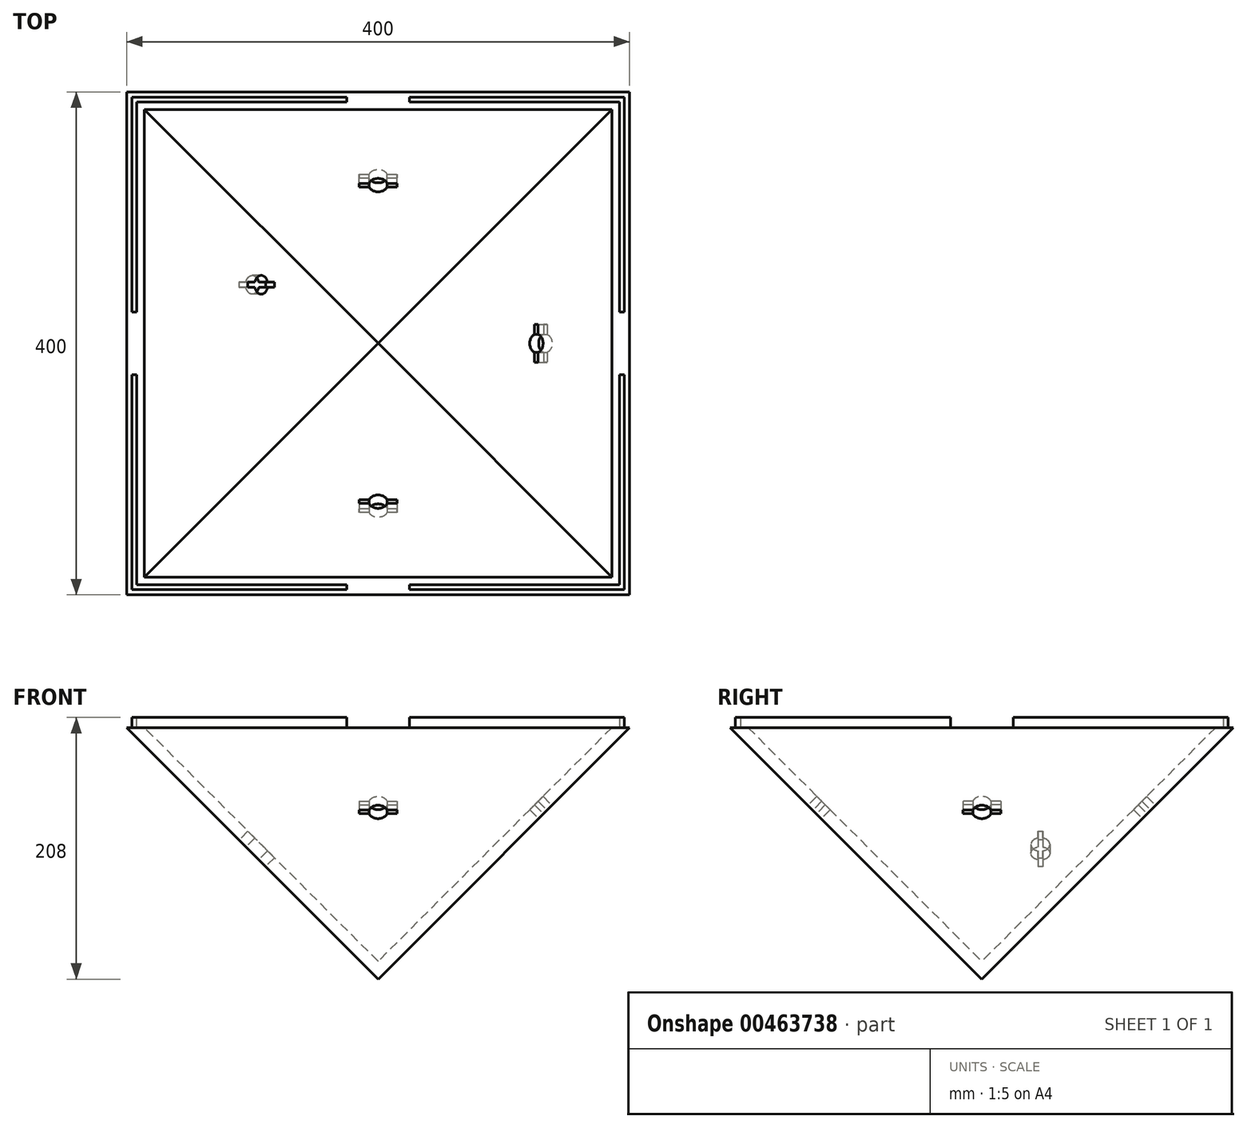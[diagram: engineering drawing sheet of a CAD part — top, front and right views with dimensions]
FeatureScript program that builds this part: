
annotation { "Feature Type Name" : "Feature", "Feature Type Description" : "" }
export const myFeature = defineFeature(function(context is Context, id is Id, definition is map)
    precondition{}
    {
        {
            var Q0;
            Q0=qCreatedBy(makeId("Top.planeOp"),FACE);
            var sketch = newSketch(context, id + "F0", { "sketchPlane" : qUnion([Q0])});
            skLineSegment(sketch, "E0.bottom", {"start": v(-200, 200) * mm, "end": v(200, 200) * mm});
            skLineSegment(sketch, "E0.top", {"start": v(-200, -200) * mm, "end": v(200, -200) * mm});
            skLineSegment(sketch, "E0.left", {"start": v(-200, 200) * mm, "end": v(-200, -200) * mm});
            skLineSegment(sketch, "E0.right", {"start": v(200, 200) * mm, "end": v(200, -200) * mm});
            skPoint(sketch, "E0.middle", {"position": v(0, 0) * mm});
            skSolve(sketch);
        }
        {
            var Q0;
            Q0=qCreatedBy(makeId("Front.planeOp"),FACE);
            var sketch = newSketch(context, id + "F1", { "sketchPlane" : qUnion([Q0])});
            skLineSegment(sketch, "E1", {"start": v(0, 0) * mm, "end": v(-200, 0) * mm});
            skLineSegment(sketch, "E2", {"start": v(0, 0) * mm, "end": v(0, -200) * mm});
            skLineSegment(sketch, "E3", {"start": v(0, -200) * mm, "end": v(-200, 0) * mm});
            skSolve(sketch);
        }
        {
            var Q0;
            Q0=makeQuery(id+"F0.imprint","IMPRINT",FACE,{"disambiguationData":[TD([[makeQuery(id+"F0.imprint","IMPRINT",EDGE,{"derivedFrom":sQuery(id+"F0.wireOp",EDGE,"E0.bottom")}),-1.0]])]});
            var Q1;
            Q1=sQuery(id+"F1.wireOp",VERTEX,"E3.start");
            loft(context, id + "F2", {"sheetProfilesArray" : [{ "sheetProfileEntities" : qUnion([Q0]) }, { "sheetProfileEntities" : qUnion([Q1]) }]});
        }
        {
            var Q0;
            Q0=makeQuery(id+"F2.opLoft","CAP_FACE",FACE,{"disambiguationData":[OSD([makeQuery(id+"F0.imprint","IMPRINT",FACE,{"disambiguationData":[TD([[makeQuery(id+"F0.imprint","IMPRINT",EDGE,{"derivedFrom":sQuery(id+"F0.wireOp",EDGE,"E0.bottom")}),-1.0]])]})])],"isStart":true});
            shell(context, id + "F3", {"entities" : qUnion([Q0]), "thickness" : 10 * mm});
        }
        {
            var Q0;
            Q0=makeQuery(id+"F0.imprint","IMPRINT",FACE,{"disambiguationData":[TD([[makeQuery(id+"F0.imprint","IMPRINT",EDGE,{"derivedFrom":sQuery(id+"F0.wireOp",EDGE,"E0.bottom")}),-1.0]])]});
            var sketch = newSketch(context, id + "F4", { "sketchPlane" : qUnion([Q0])});
            skLineSegment(sketch, "E4.0", {"start": v(-191.86, 191.86) * mm, "end": v(191.86, 191.86) * mm});
            skLineSegment(sketch, "E4.1", {"start": v(-191.86, -191.86) * mm, "end": v(-191.86, 191.86) * mm});
            skLineSegment(sketch, "E4.2", {"start": v(191.86, -191.86) * mm, "end": v(-191.86, -191.86) * mm});
            skLineSegment(sketch, "E4.3", {"start": v(191.86, 191.86) * mm, "end": v(191.86, -191.86) * mm});
            skLineSegment(sketch, "E5.0", {"start": v(-195.86, 195.86) * mm, "end": v(195.86, 195.86) * mm});
            skLineSegment(sketch, "E5.1", {"start": v(-195.86, -195.86) * mm, "end": v(-195.86, 195.86) * mm});
            skLineSegment(sketch, "E5.2", {"start": v(195.86, -195.86) * mm, "end": v(-195.86, -195.86) * mm});
            skLineSegment(sketch, "E5.3", {"start": v(195.86, 195.86) * mm, "end": v(195.86, -195.86) * mm});
            skSolve(sketch);
        }
        {
            var Q0;
            Q0=makeQuery(id+"F4.imprint","IMPRINT",FACE,{"disambiguationData":[TD([[makeQuery(id+"F4.imprint","IMPRINT",EDGE,{"derivedFrom":sQuery(id+"F4.wireOp",EDGE,"E4.0")}),1.0]])]});
            extrude(context, id + "F5", {"entities" : qUnion([Q0]), "operationType" : NewBodyOperationType.ADD, "depth" : 8 * mm});
        }
        {
            var Q0;
            Q0=makeQuery(id+"F2.opLoft","SWEPT_FACE",FACE,{"disambiguationData":[OSD([sQuery(id+"F0.wireOp",EDGE,"E0.top"),sQuery(id+"F0.wireOp",EDGE,"E0.left"),sQuery(id+"F0.wireOp",EDGE,"E0.right")])]});
            var sketch = newSketch(context, id + "F6", { "sketchPlane" : qUnion([Q0])});
            skLineSegment(sketch, "E6", {"start": v(0, -141.42) * mm, "end": v(0, 46.58) * mm});
            skLineSegment(sketch, "E7", {"start": v(0, 46.58) * mm, "end": v(7.5, 46.58) * mm});
            skCircle(sketch, "E8", {"center": v(0, 46.58) * mm, "radius": 7.5 * mm});
            skLineSegment(sketch, "E9.bottom", {"start": v(15, 48.58) * mm, "end": v(-15, 48.58) * mm});
            skLineSegment(sketch, "E9.top", {"start": v(15, 44.58) * mm, "end": v(-15, 44.58) * mm});
            skLineSegment(sketch, "E9.left", {"start": v(15, 48.58) * mm, "end": v(15, 44.58) * mm});
            skLineSegment(sketch, "E9.right", {"start": v(-15, 48.58) * mm, "end": v(-15, 44.58) * mm});
            skSolve(sketch);
        }
        {
            var Q0;
            Q0=makeQuery(id+"F2.opLoft","SWEPT_FACE",FACE,{"disambiguationData":[OSD([sQuery(id+"F0.wireOp",EDGE,"E0.bottom"),sQuery(id+"F0.wireOp",EDGE,"E0.top"),sQuery(id+"F0.wireOp",EDGE,"E0.right")])]});
            var sketch = newSketch(context, id + "F7", { "sketchPlane" : qUnion([Q0])});
            skLineSegment(sketch, "E10", {"start": v(0, -141.42) * mm, "end": v(0, 46.58) * mm});
            skLineSegment(sketch, "E11", {"start": v(0, 46.58) * mm, "end": v(7.5, 46.58) * mm});
            skCircle(sketch, "E12", {"center": v(0, 46.58) * mm, "radius": 7.5 * mm});
            skLineSegment(sketch, "E13.bottom", {"start": v(15, 48.58) * mm, "end": v(-15, 48.58) * mm});
            skLineSegment(sketch, "E13.top", {"start": v(15, 44.58) * mm, "end": v(-15, 44.58) * mm});
            skLineSegment(sketch, "E13.left", {"start": v(15, 48.58) * mm, "end": v(15, 44.58) * mm});
            skLineSegment(sketch, "E13.right", {"start": v(-15, 48.58) * mm, "end": v(-15, 44.58) * mm});
            skSolve(sketch);
        }
        {
            var Q0;
            Q0=makeQuery(id+"F2.opLoft","SWEPT_FACE",FACE,{"disambiguationData":[OSD([sQuery(id+"F0.wireOp",EDGE,"E0.bottom"),sQuery(id+"F0.wireOp",EDGE,"E0.left"),sQuery(id+"F0.wireOp",EDGE,"E0.right")])]});
            var sketch = newSketch(context, id + "F8", { "sketchPlane" : qUnion([Q0])});
            skLineSegment(sketch, "E14", {"start": v(0, -141.42) * mm, "end": v(0, 46.58) * mm});
            skLineSegment(sketch, "E15", {"start": v(0, 46.58) * mm, "end": v(7.5, 46.58) * mm});
            skCircle(sketch, "E16", {"center": v(0, 46.58) * mm, "radius": 7.5 * mm});
            skLineSegment(sketch, "E17.bottom", {"start": v(15, 48.58) * mm, "end": v(-15, 48.58) * mm});
            skLineSegment(sketch, "E17.top", {"start": v(15, 44.58) * mm, "end": v(-15, 44.58) * mm});
            skLineSegment(sketch, "E17.left", {"start": v(15, 48.58) * mm, "end": v(15, 44.58) * mm});
            skLineSegment(sketch, "E17.right", {"start": v(-15, 48.58) * mm, "end": v(-15, 44.58) * mm});
            skSolve(sketch);
        }
        {
            var Q0;
            Q0=makeQuery(id+"F2.opLoft","SWEPT_FACE",FACE,{"disambiguationData":[OSD([sQuery(id+"F0.wireOp",EDGE,"E0.bottom"),sQuery(id+"F0.wireOp",EDGE,"E0.top"),sQuery(id+"F0.wireOp",EDGE,"E0.left")])]});
            var sketch = newSketch(context, id + "F9", { "sketchPlane" : qUnion([Q0])});
            skLineSegment(sketch, "E18", {"start": v(141.42, 0) * mm, "end": v(-46.58, 0) * mm});
            skCircle(sketch, "E19", {"center": v(-46.58, 0) * mm, "radius": 7.5 * mm});
            skLineSegment(sketch, "E20.bottom", {"start": v(-48.58, 15) * mm, "end": v(-44.58, 15) * mm});
            skLineSegment(sketch, "E20.top", {"start": v(-48.58, -15) * mm, "end": v(-44.58, -15) * mm});
            skLineSegment(sketch, "E20.left", {"start": v(-48.58, 15) * mm, "end": v(-48.58, -15) * mm});
            skLineSegment(sketch, "E20.right", {"start": v(-44.58, 15) * mm, "end": v(-44.58, -15) * mm});
            skSolve(sketch);
        }
        {
            var Q0;
            Q0 = qSketchRegion(id + "F6", true);
            extrude(context, id + "F10", {"entities" : qUnion([Q0]), "operationType" : NewBodyOperationType.REMOVE, "endBound" : BoundingType.THROUGH_ALL, "oppositeDirection" : true, "depth" : 25 * mm});
        }
        {
            var Q0;
            Q0 = qSketchRegion(id + "F7", true);
            extrude(context, id + "F11", {"entities" : qUnion([Q0]), "operationType" : NewBodyOperationType.REMOVE, "endBound" : BoundingType.THROUGH_ALL, "oppositeDirection" : true, "depth" : 25 * mm});
        }
        {
            var Q0;
            Q0 = qSketchRegion(id + "F8", true);
            extrude(context, id + "F12", {"entities" : qUnion([Q0]), "operationType" : NewBodyOperationType.REMOVE, "endBound" : BoundingType.THROUGH_ALL, "oppositeDirection" : true, "depth" : 25 * mm});
        }
        {
            var Q0;
            Q0 = qSketchRegion(id + "F9", true);
            extrude(context, id + "F13", {"entities" : qUnion([Q0]), "operationType" : NewBodyOperationType.REMOVE, "endBound" : BoundingType.THROUGH_ALL, "oppositeDirection" : true, "depth" : 25 * mm});
        }
        {
            var Q0;
            Q0=makeQuery(id+"F5.opExtrude","SWEPT_FACE",FACE,{"disambiguationData":[OSD([sQuery(id+"F4.wireOp",EDGE,"E5.2")])]});
            var sketch = newSketch(context, id + "F14", { "sketchPlane" : qUnion([Q0])});
            skLineSegment(sketch, "E21", {"start": v(0, 0) * mm, "end": v(0, 8) * mm});
            skLineSegment(sketch, "E22.bottom", {"start": v(25, 8) * mm, "end": v(-25, 8) * mm});
            skLineSegment(sketch, "E22.top", {"start": v(25, 0) * mm, "end": v(-25, 0) * mm});
            skLineSegment(sketch, "E22.left", {"start": v(25, 8) * mm, "end": v(25, 0) * mm});
            skLineSegment(sketch, "E22.right", {"start": v(-25, 8) * mm, "end": v(-25, 0) * mm});
            skPoint(sketch, "E22.middle", {"position": v(0, 4) * mm});
            skSolve(sketch);
        }
        {
            var Q0;
            Q0 = qSketchRegion(id + "F14", true);
            extrude(context, id + "F15", {"entities" : qUnion([Q0]), "operationType" : NewBodyOperationType.REMOVE, "endBound" : BoundingType.THROUGH_ALL, "oppositeDirection" : true, "depth" : 25 * mm});
        }
        {
            var Q0;
            Q0=makeQuery(id+"F5.opExtrude","SWEPT_FACE",FACE,{"disambiguationData":[OSD([sQuery(id+"F4.wireOp",EDGE,"E5.1")])]});
            var sketch = newSketch(context, id + "F16", { "sketchPlane" : qUnion([Q0])});
            skLineSegment(sketch, "E23", {"start": v(0, 0) * mm, "end": v(0, 8) * mm});
            skLineSegment(sketch, "E24.bottom", {"start": v(25, 0) * mm, "end": v(-25, 0) * mm});
            skLineSegment(sketch, "E24.top", {"start": v(25, 8) * mm, "end": v(-25, 8) * mm});
            skLineSegment(sketch, "E24.left", {"start": v(25, 0) * mm, "end": v(25, 8) * mm});
            skLineSegment(sketch, "E24.right", {"start": v(-25, 0) * mm, "end": v(-25, 8) * mm});
            skPoint(sketch, "E24.middle", {"position": v(0, 4) * mm});
            skSolve(sketch);
        }
        {
            var Q0;
            Q0 = qSketchRegion(id + "F16", true);
            extrude(context, id + "F17", {"entities" : qUnion([Q0]), "operationType" : NewBodyOperationType.REMOVE, "endBound" : BoundingType.THROUGH_ALL, "oppositeDirection" : true, "depth" : 25 * mm});
        }
    });
